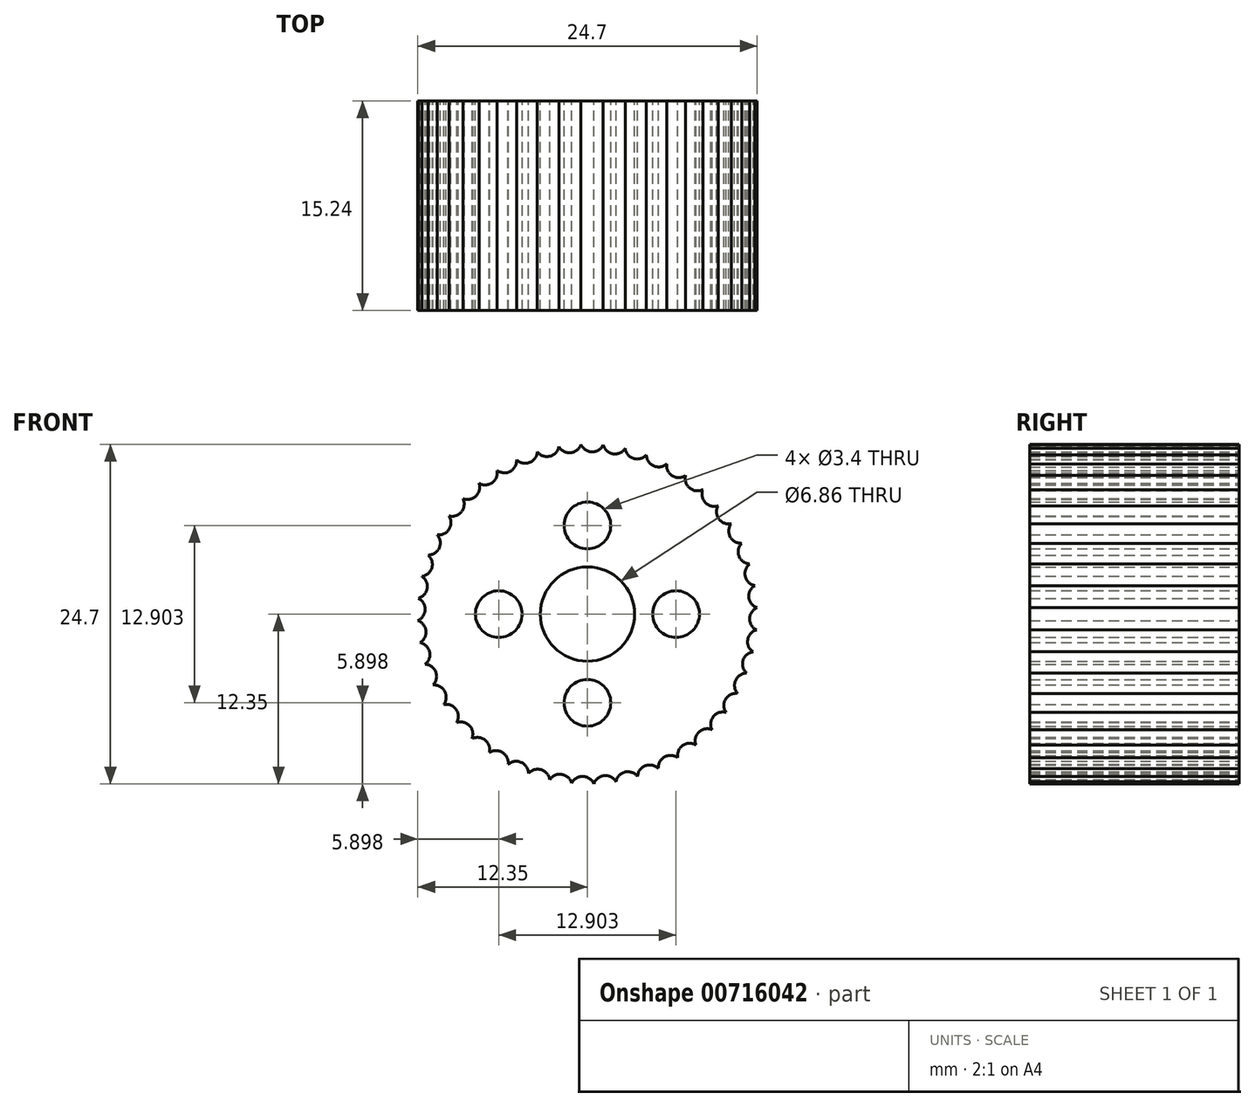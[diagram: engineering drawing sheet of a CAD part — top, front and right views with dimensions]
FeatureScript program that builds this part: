
annotation { "Feature Type Name" : "Feature", "Feature Type Description" : "" }
export const myFeature = defineFeature(function(context is Context, id is Id, definition is map)
    precondition{}
    {
        {
            var Q0;
            Q0=qCreatedBy(makeId("Front.planeOp"),FACE);
            var sketch = newSketch(context, id + "F0", { "sketchPlane" : qUnion([Q0])});
            skCircle(sketch, "E0", {"center": v(0, 0) * mm, "radius": 3.43 * mm});
            skCircle(sketch, "E1", {"center": v(0, 6.45) * mm, "radius": 1.7 * mm});
            skCircle(sketch, "E2", {"center": v(6.45, 0) * mm, "radius": 1.7 * mm});
            skCircle(sketch, "E3", {"center": v(0, -6.45) * mm, "radius": 1.7 * mm});
            skCircle(sketch, "E4", {"center": v(-6.45, 0) * mm, "radius": 1.7 * mm});
            skCircle(sketch, "E5", {"center": v(0, 0) * mm, "radius": 12.7 * mm});
            skSolve(sketch);
        }
        {
            var Q0;
            Q0=qSketchRegion(id+"F0",true);
            extrude(context, id + "F1", {"entities" : qUnion([Q0]), "depth" : 15.24 * mm, "offsetDistance" : 25.4 * mm});
        }
        {
            var Q0;
            Q0=qCreatedBy(makeId("Right.planeOp"),FACE);
            var sketch = newSketch(context, id + "F2", { "sketchPlane" : qUnion([Q0])});
            skLineSegment(sketch, "E6", {"start": v(24.8, 0) * mm, "end": v(-23.69, 0) * mm});
            skSolve(sketch);
        }
        {
            var Q0;
            Q0=makeQuery(id+"F1.opExtrude","CAP_FACE",FACE,{"disambiguationData":[OSD([sQuery(id+"F0.wireOp",EDGE,"E0"),sQuery(id+"F0.wireOp",EDGE,"E1"),sQuery(id+"F0.wireOp",EDGE,"E2"),sQuery(id+"F0.wireOp",EDGE,"E3"),sQuery(id+"F0.wireOp",EDGE,"E4"),sQuery(id+"F0.wireOp",EDGE,"E5")])],"isStart":false});
            var sketch = newSketch(context, id + "F3", { "sketchPlane" : qUnion([Q0])});
            skCircle(sketch, "E7", {"center": v(-7.45, 10.29) * mm, "radius": 0.89 * mm});
            skSolve(sketch);
        }
        {
            var Q0;
            Q0=qSketchRegion(id+"F3",true);
            extrude(context, id + "F4", {"entities" : qUnion([Q0]), "endBound" : BoundingType.SYMMETRIC, "depth" : 50.8 * mm, "offsetDistance" : 25.4 * mm});
        }
        {
            var Q0;
            Q0=makeQuery(id+"F4.opExtrude","SWEPT_BODY",BODY,{"disambiguationData":[OSD([sQuery(id+"F3.wireOp",EDGE,"E7")])]});
            var Q1;
            Q1=sQuery(id+"F2.wireOp",EDGE,"E6");
            circularPattern(context, id + "F5", {"operationType" : NewBodyOperationType.REMOVE, "entities" : qUnion([Q0]), "axis" : qUnion([Q1]), "angle" : 360 * degree, "instanceCount" : 48, "equalSpace" : true});
        }
    });
